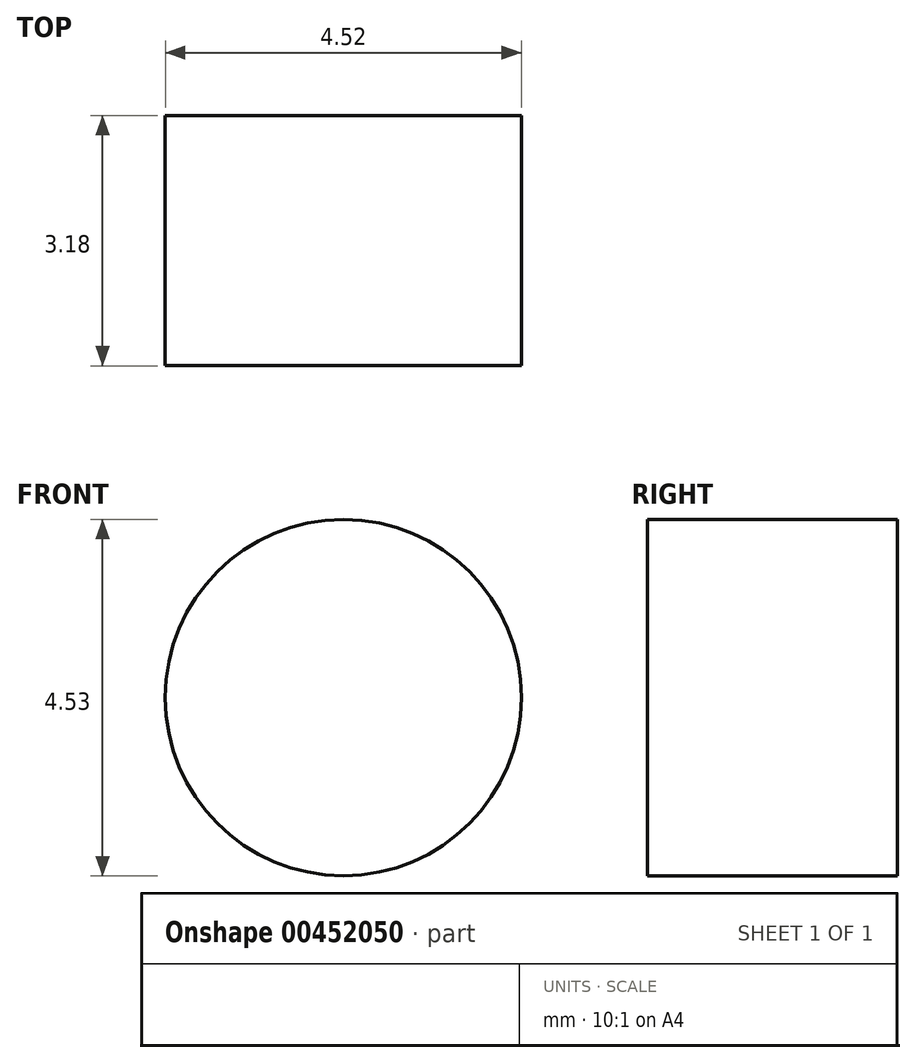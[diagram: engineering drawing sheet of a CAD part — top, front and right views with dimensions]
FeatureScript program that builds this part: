
annotation { "Feature Type Name" : "Feature", "Feature Type Description" : "" }
export const myFeature = defineFeature(function(context is Context, id is Id, definition is map)
    precondition{}
    {
        {
            var Q0;
            Q0=qCreatedBy(makeId("Front.planeOp"),FACE);
            var sketch = newSketch(context, id + "F0", { "sketchPlane" : qUnion([Q0])});
            skLineSegment(sketch, "E0.bottom", {"start": v(-101.46, 106.61) * mm, "end": v(0.14, 106.61) * mm});
            skLineSegment(sketch, "E0.top", {"start": v(-101.46, -20.39) * mm, "end": v(0.14, -20.39) * mm});
            skLineSegment(sketch, "E0.left", {"start": v(-101.46, 106.61) * mm, "end": v(-101.46, -20.39) * mm});
            skLineSegment(sketch, "E0.right", {"start": v(0.14, 106.61) * mm, "end": v(0.14, -20.39) * mm});
            skSolve(sketch);
        }
        {
            var Q0;
            Q0 = qSketchRegion(id + "F0", true);
            extrude(context, id + "F1", {"entities" : qUnion([Q0]), "depth" : 3.17 * mm});
        }
        {
            var Q0;
            Q0=makeQuery(id+"F1.opExtrude","CAP_FACE",FACE,{"disambiguationData":[OSD([sQuery(id+"F0.wireOp",EDGE,"E0.bottom"),sQuery(id+"F0.wireOp",EDGE,"E0.top"),sQuery(id+"F0.wireOp",EDGE,"E0.left"),sQuery(id+"F0.wireOp",EDGE,"E0.right")])],"isStart":false});
            var sketch = newSketch(context, id + "F2", { "sketchPlane" : qUnion([Q0])});
            skLineSegment(sketch, "E1", {"start": v(-101.46, 47.08) * mm, "end": v(0, 47.08) * mm, "construction": true});
            skCircle(sketch, "E2", {"center": v(-50.66, 14.3) * mm, "radius": 2.26 * mm});
            skCircle(sketch, "E3.MirrorC", {"center": v(-50.66, 79.88) * mm, "radius": 2.26 * mm});
            skLineSegment(sketch, "E4", {"start": v(-50.66, 79.88) * mm, "end": v(-50.66, 14.3) * mm, "construction": true});
            skSolve(sketch);
        }
        {
            var Q0;
            Q0=makeQuery(id+"F2.imprint","IMPRINT",FACE,{"disambiguationData":[TD([[makeQuery(id+"F2.imprint","IMPRINT",EDGE,{"derivedFrom":sQuery(id+"F2.wireOp",EDGE,"E3.MirrorC")}),-1.0]])]});
            var Q1;
            Q1=makeQuery(id+"F2.imprint","IMPRINT",FACE,{"disambiguationData":[TD([[makeQuery(id+"F2.imprint","IMPRINT",EDGE,{"derivedFrom":sQuery(id+"F2.wireOp",EDGE,"E2")}),1.0]])]});
            extrude(context, id + "F3", {"entities" : qUnion([Q0, Q1]), "operationType" : NewBodyOperationType.REMOVE, "endBound" : BoundingType.THROUGH_ALL, "oppositeDirection" : true, "depth" : 25.4 * mm});
        }
        {
            var Q0;
            Q0=makeQuery(id+"F1.opExtrude","CAP_FACE",FACE,{"disambiguationData":[OSD([sQuery(id+"F0.wireOp",EDGE,"E0.bottom"),sQuery(id+"F0.wireOp",EDGE,"E0.top"),sQuery(id+"F0.wireOp",EDGE,"E0.left"),sQuery(id+"F0.wireOp",EDGE,"E0.right")])],"isStart":false});
            var sketch = newSketch(context, id + "F4", { "sketchPlane" : qUnion([Q0])});
            skCircle(sketch, "E5", {"center": v(-92.78, 59.78) * mm, "radius": 3.18 * mm});
            skCircle(sketch, "E6", {"center": v(-92.78, 34.38) * mm, "radius": 3.18 * mm});
            skCircle(sketch, "E7.MirrorC", {"center": v(-8.54, 34.38) * mm, "radius": 3.18 * mm});
            skCircle(sketch, "E8.MirrorC", {"center": v(-8.54, 59.78) * mm, "radius": 3.18 * mm});
            skSolve(sketch);
        }
        {
            var Q0;
            Q0 = qSketchRegion(id + "F4", true);
            extrude(context, id + "F5", {"entities" : qUnion([Q0]), "operationType" : NewBodyOperationType.REMOVE, "endBound" : BoundingType.THROUGH_ALL, "oppositeDirection" : true, "depth" : 25.4 * mm});
        }
    });
